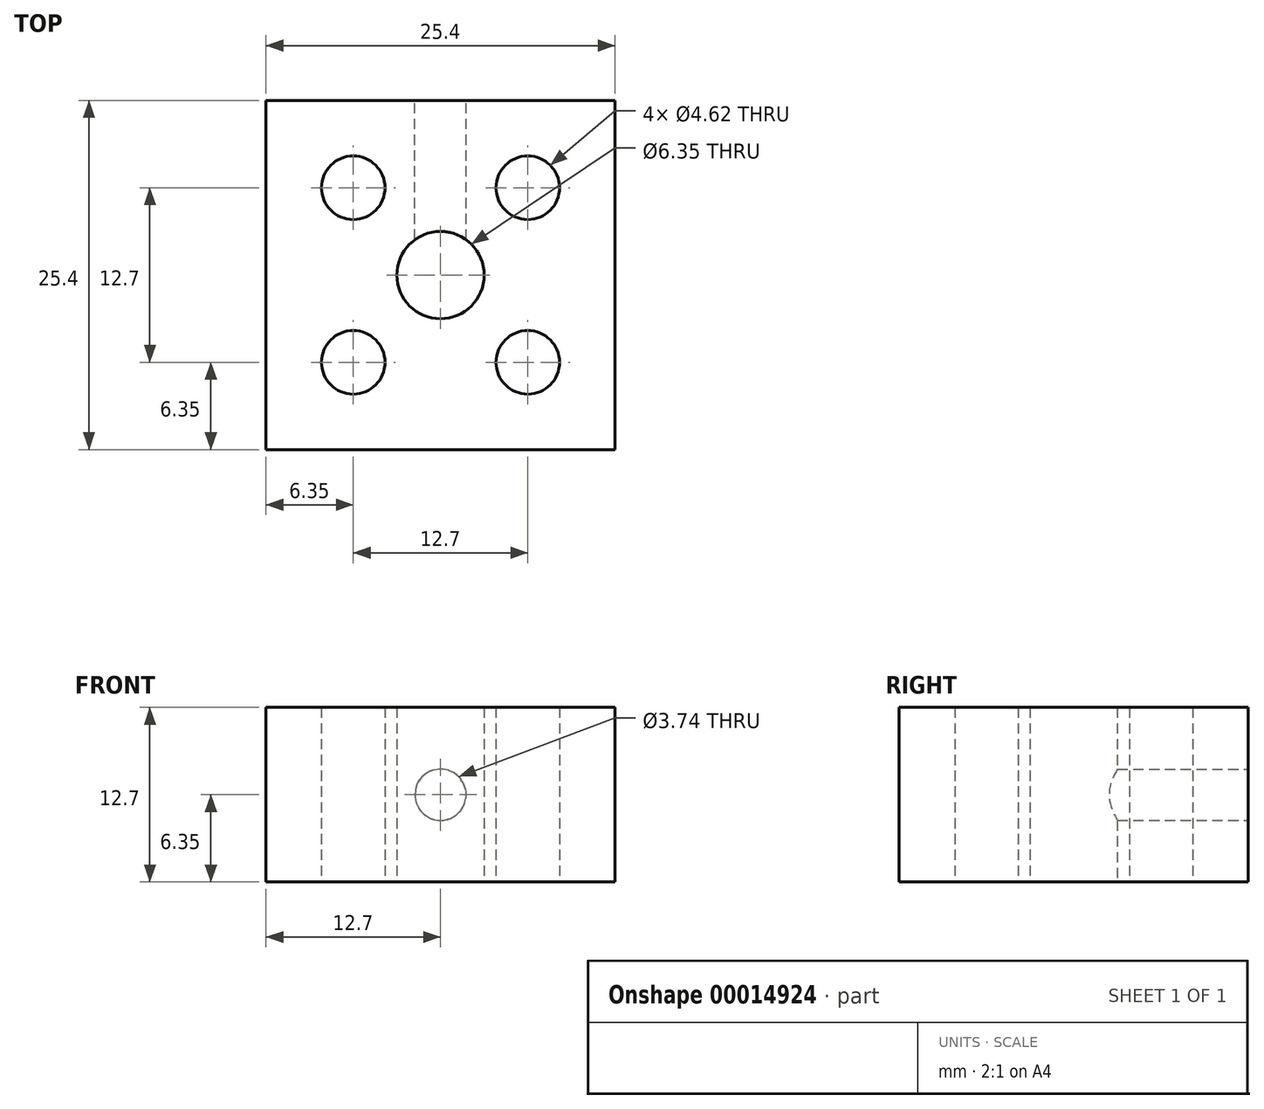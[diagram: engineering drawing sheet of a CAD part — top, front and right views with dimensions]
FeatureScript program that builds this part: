
annotation { "Feature Type Name" : "Feature", "Feature Type Description" : "" }
export const myFeature = defineFeature(function(context is Context, id is Id, definition is map)
    precondition{}
    {
        {
            var Q0;
            Q0=qCreatedBy(makeId("Top.planeOp"),FACE);
            var sketch = newSketch(context, id + "F0", { "sketchPlane" : qUnion([Q0])});
            skLineSegment(sketch, "E0.bottom", {"start": v(0, 0) * mm, "end": v(25.4, 0) * mm});
            skLineSegment(sketch, "E0.top", {"start": v(0, 25.4) * mm, "end": v(25.4, 25.4) * mm});
            skLineSegment(sketch, "E0.left", {"start": v(0, 0) * mm, "end": v(0, 25.4) * mm});
            skLineSegment(sketch, "E0.right", {"start": v(25.4, 0) * mm, "end": v(25.4, 25.4) * mm});
            skCircle(sketch, "E1", {"center": v(12.7, 12.7) * mm, "radius": 3.18 * mm});
            skCircle(sketch, "E2", {"center": v(6.35, 6.35) * mm, "radius": 2.31 * mm});
            skCircle(sketch, "E3", {"center": v(19.05, 6.35) * mm, "radius": 2.31 * mm});
            skCircle(sketch, "E4", {"center": v(19.05, 19.05) * mm, "radius": 2.31 * mm});
            skCircle(sketch, "E5", {"center": v(6.35, 19.05) * mm, "radius": 2.31 * mm});
            skCircle(sketch, "E6", {"center": v(12.7, 12.7) * mm, "radius": 11.3 * mm});
            skSolve(sketch);
        }
        {
            var Q0;
            Q0=makeQuery(id+"F0.imprint","IMPRINT",FACE,{"disambiguationData":[TD([[makeQuery(id+"F0.imprint","IMPRINT",EDGE,{"derivedFrom":sQuery(id+"F0.wireOp",EDGE,"E0.bottom")}),1.0]])]});
            var Q1;
            Q1=makeQuery(id+"F0.imprint","IMPRINT",FACE,{"disambiguationData":[TD([[makeQuery(id+"F0.imprint","IMPRINT",EDGE,{"derivedFrom":sQuery(id+"F0.wireOp",EDGE,"E1")}),-1.0]])]});
            extrude(context, id + "F1", {"entities" : qUnion([Q0, Q1]), "depth" : 12.7 * mm});
        }
        {
            var Q0;
            Q0=makeQuery(id+"F1.opExtrude","SWEPT_FACE",FACE,{"disambiguationData":[OSD([sQuery(id+"F0.wireOp",EDGE,"E0.top")])]});
            var sketch = newSketch(context, id + "F2", { "sketchPlane" : qUnion([Q0])});
            skCircle(sketch, "E7", {"center": v(-12.7, 6.35) * mm, "radius": 1.87 * mm});
            skSolve(sketch);
        }
        {
            var Q0;
            Q0=makeQuery(id+"F2.imprint","IMPRINT",FACE,{"disambiguationData":[TD([[makeQuery(id+"F2.imprint","IMPRINT",EDGE,{"derivedFrom":sQuery(id+"F2.wireOp",EDGE,"E7")}),1.0]])]});
            extrude(context, id + "F3", {"entities" : qUnion([Q0]), "operationType" : NewBodyOperationType.REMOVE, "oppositeDirection" : true, "depth" : 12.7 * mm});
        }
    });
